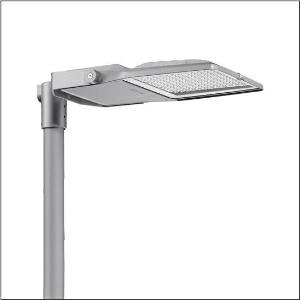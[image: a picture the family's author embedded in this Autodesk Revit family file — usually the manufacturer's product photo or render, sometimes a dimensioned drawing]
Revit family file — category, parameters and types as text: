
# Revit family: floodlight_fl_21_iq_midi___pl33t_5xa7782e2f3a_552b
name_source: partatom
category: Lighting Fixtures
units: mm (PartAtom-declared; Revit-internal decimal feet)

## family parameters
Cut with Voids When Loaded = No
Host = Face
Light Source = No
Part Type = Normal
Room Calculation Point = No
Round Connector Dimension = Use Diameter
Shared = No

## types (1)
- --- (1 x LED, 26540 lm, 208.1 W, 3000K)
    Apparent Load = 208 VA
    CIE Flux Codes = 26 75 99 100 100
    Color Rendering = 70
    Color Temperature = 3000K
    Default Elevation = 1800 mm
    Description = Floodlight FL 21 iQ midi, floodlight, primary light control with lens, of PMMA, primary optical cover: protective disc, of toughened safety glass, transparent, light distribution: PL33T, light emission: direct distribution, installation type: surface-mounted, LED, High Power LED, rated luminous flux: 26.540lm, luminous efficacy: 128lm/W, light colour: 730, colour temperature: 3000K, control gear: ECG iQ, control: optimised constant luminous flux control (CLO 2.0), Desk-Remote (wireless, voltage-free reading and setting of iQ features in the workshop via application-optimized NFC function/RFID function), Smart-Wire, Night-Set, Temp-Guard, Auto-Match, Street-Remote, with terminal, 6-pole, mains connection: 220..240V, AC, 50/60Hz, start of lifetime: 208W, end of service life: 227W, reduction: 90W, luminaire housing, of diecast aluminium, powder-coated, Siteco® metallic grey (DB 702S), corrosivity category C5 mid according to DIN EN ISO 12944, sealing non-destructively replaceable, please order mast flange separately, mast bracket, of steel, galvanised, powder-coated, Siteco® metallic grey (DB 702S), protection rating (complete): IP66, insulation class (complete): insulation class II (safety insulation), certification: CE, ENEC, VDE, protection symbol: D, impact resistance: IK08, permissible operating ambient temperature: -40..+40°C, permissible operating ambient temperature for outdoor applications: -40..+50°C, standard: DIN EN 12944, LABS conformity tested according to VDMA 24364:2018-05, packaging unit: 1 piece

Light Distribution: PL33T
    Height = 76 mm
    Lamp = 1 x LED
    Lamp Light Flux = 26540 lm
    Lamp Power = 208.1 W
    Lamp count = 1
    Length = 657 mm
    Luminous efficacy = 128 lm/W
    Manufacturer = Siteco
    ModVariant = No
    Model = 5XA7782E2F3A
    Number of Poles = 1
    OnlyDefault = Yes
    Power Factor = 1
    Product Name = Floodlight FL 21 iQ midi | PL33T
    Product group = floodlight | pylon annexe
    ProductGroupID = 6200
    Protection Class = Protection class II
    Protection Degree = IP 66
    RLX_Detail_Level = 1
    RLX_Emergency_Light_Flux = 0 lm
    RLX_Emergency_Type = 0
    RLX_Emergency_Type_DB = No
    RlxData = <blob elided: 153589 chars, md5=7acf42cf>
    Socket = socket
    Standby Power = 0 W
    System Light Flux = 26540 lm
    System Power = 208 W
    Type Comments = factory setting: luminous flux: 100 % | dim-lin: 254 | 710 mA
    Type Image = l_1007123.jpg
    URL = http://relux.com
    VarID = @adj_072677
    Voltage = 0 V
    Weight = 0.00 kg
    Width = 442 mm

## geometry (parser evidence)
native form markers: Blend x4, Sweep x12
no freeform markers — native parametric forms only
